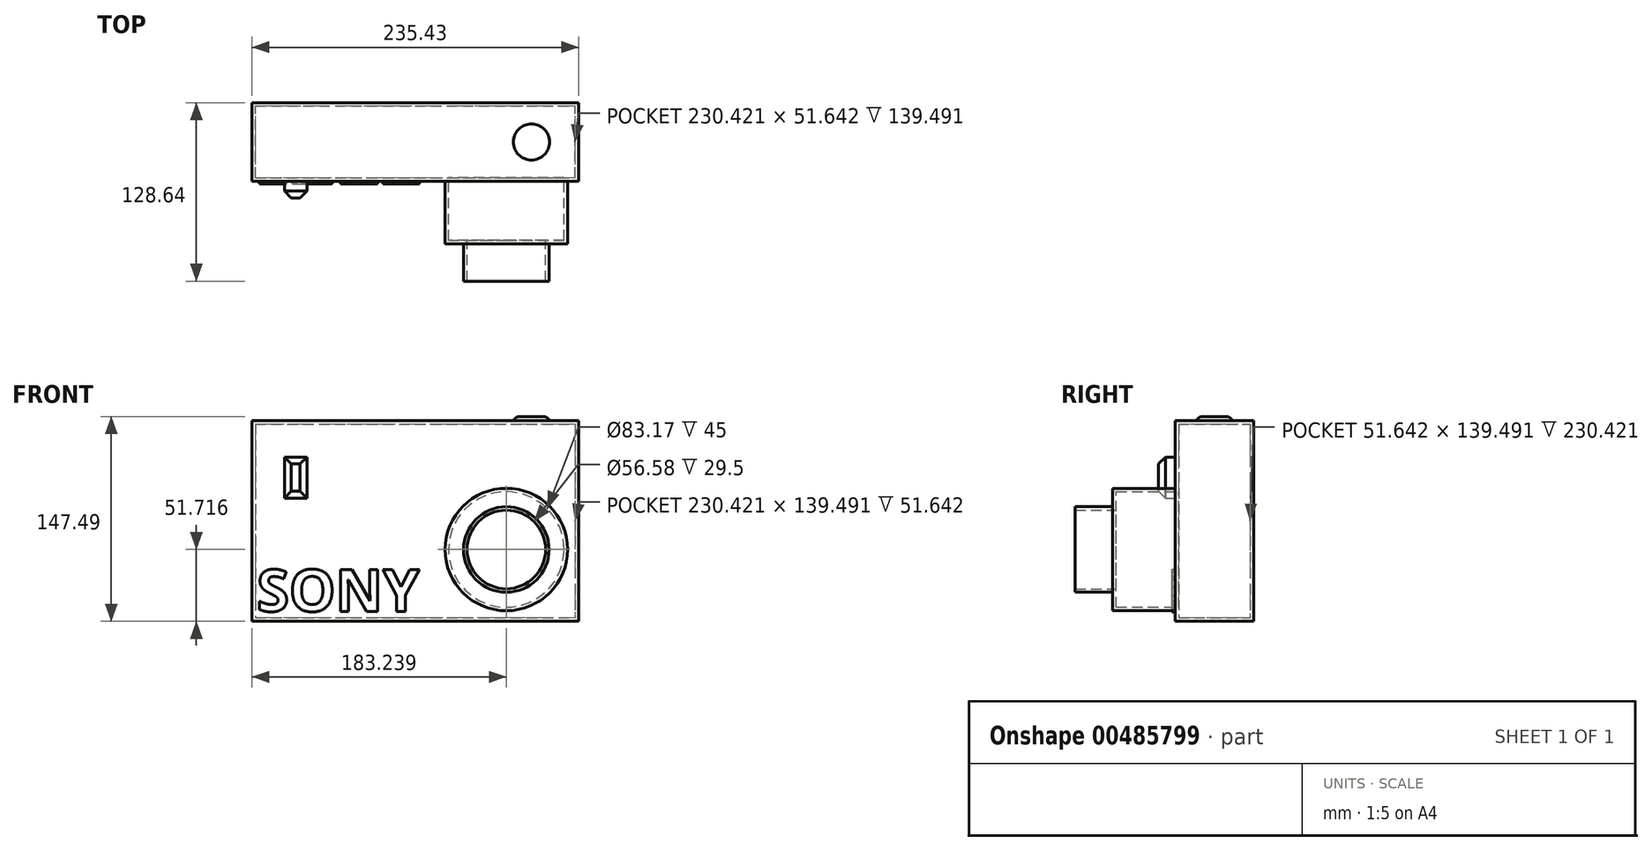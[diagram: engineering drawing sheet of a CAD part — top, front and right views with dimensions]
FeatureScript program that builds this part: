
annotation { "Feature Type Name" : "Feature", "Feature Type Description" : "" }
export const myFeature = defineFeature(function(context is Context, id is Id, definition is map)
    precondition{}
    {
        {
            var Q0;
            Q0=qCreatedBy(makeId("Front.planeOp"),FACE);
            var sketch = newSketch(context, id + "F0", { "sketchPlane" : qUnion([Q0])});
            skLineSegment(sketch, "E0.bottom", {"start": v(-116.88, 70.73) * mm, "end": v(118.55, 70.73) * mm});
            skLineSegment(sketch, "E0.top", {"start": v(-116.88, -73.76) * mm, "end": v(118.55, -73.76) * mm});
            skLineSegment(sketch, "E0.left", {"start": v(-116.88, 70.73) * mm, "end": v(-116.88, -73.76) * mm});
            skLineSegment(sketch, "E0.right", {"start": v(118.55, 70.73) * mm, "end": v(118.55, -73.76) * mm});
            skSolve(sketch);
        }
        {
            var Q0;
            Q0 = qSketchRegion(id + "F0", true);
            extrude(context, id + "F1", {"entities" : qUnion([Q0]), "depth" : 56.64 * mm});
        }
        {
            var Q0;
            Q0=makeQuery(id+"F1.opExtrude","CAP_FACE",FACE,{"disambiguationData":[OSD([sQuery(id+"F0.wireOp",EDGE,"E0.bottom"),sQuery(id+"F0.wireOp",EDGE,"E0.top"),sQuery(id+"F0.wireOp",EDGE,"E0.left"),sQuery(id+"F0.wireOp",EDGE,"E0.right")])],"isStart":false});
            var sketch = newSketch(context, id + "F2", { "sketchPlane" : qUnion([Q0])});
            skCircle(sketch, "E1", {"center": v(66.36, -22.04) * mm, "radius": 44.08 * mm});
            skSolve(sketch);
        }
        {
            var Q0;
            Q0 = qSketchRegion(id + "F2", true);
            extrude(context, id + "F3", {"entities" : qUnion([Q0]), "operationType" : NewBodyOperationType.ADD, "depth" : 45 * mm});
        }
        {
            var Q0;
            Q0=makeQuery(id+"F3.opExtrude","CAP_FACE",FACE,{"disambiguationData":[OSD([sQuery(id+"F2.wireOp",EDGE,"E1")])],"isStart":false});
            var sketch = newSketch(context, id + "F4", { "sketchPlane" : qUnion([Q0])});
            skCircle(sketch, "E2", {"center": v(66.36, -22.04) * mm, "radius": 30.8 * mm});
            skSolve(sketch);
        }
        {
            var Q0;
            Q0 = qSketchRegion(id + "F4", true);
            extrude(context, id + "F5", {"entities" : qUnion([Q0]), "operationType" : NewBodyOperationType.ADD, "depth" : 27 * mm});
        }
        {
            var Q0;
            Q0=makeQuery(id+"F5.opExtrude","CAP_FACE",FACE,{"disambiguationData":[OSD([sQuery(id+"F4.wireOp",EDGE,"E2")])],"isStart":false});
            shell(context, id + "F6", {"entities" : qUnion([Q0]), "thickness" : 2.5 * mm});
        }
        {
            var Q0;
            Q0=makeQuery(id+"F1.opExtrude","SWEPT_FACE",FACE,{"disambiguationData":[OSD([sQuery(id+"F0.wireOp",EDGE,"E0.bottom")])]});
            var sketch = newSketch(context, id + "F7", { "sketchPlane" : qUnion([Q0])});
            skCircle(sketch, "E3", {"center": v(84.46, -28.32) * mm, "radius": 13.02 * mm});
            skPoint(sketch, "E3.centerSnap0", {"position": v(118.55, -28.32) * mm});
            skSolve(sketch);
        }
        {
            var Q0;
            Q0 = qSketchRegion(id + "F7", true);
            extrude(context, id + "F8", {"entities" : qUnion([Q0]), "operationType" : NewBodyOperationType.ADD, "depth" : 3 * mm});
        }
        {
            var Q0;
            Q0=makeQuery(id+"F8.opExtrude","CAP_EDGE",EDGE,{"disambiguationData":[OSD([sQuery(id+"F7.wireOp",EDGE,"E3")])],"isStart":false});
            fillet(context, id + "F9", {"entities" : qUnion([Q0]), "radius" : 5 * mm, "tangentPropagation" : true, "allowEdgeOverflow" : false});
        }
        {
            var Q0;
            Q0=makeQuery(id+"F1.opExtrude","CAP_FACE",FACE,{"disambiguationData":[OSD([sQuery(id+"F0.wireOp",EDGE,"E0.bottom"),sQuery(id+"F0.wireOp",EDGE,"E0.top"),sQuery(id+"F0.wireOp",EDGE,"E0.left"),sQuery(id+"F0.wireOp",EDGE,"E0.right")])],"isStart":false});
            var sketch = newSketch(context, id + "F10", { "sketchPlane" : qUnion([Q0])});
            skLineSegment(sketch, "E4.bottom", {"start": v(-93.43, 44.56) * mm, "end": v(-77.07, 44.56) * mm});
            skLineSegment(sketch, "E4.top", {"start": v(-93.43, 14.96) * mm, "end": v(-77.07, 14.96) * mm});
            skLineSegment(sketch, "E4.left", {"start": v(-93.43, 44.56) * mm, "end": v(-93.43, 14.96) * mm});
            skLineSegment(sketch, "E4.right", {"start": v(-77.07, 44.56) * mm, "end": v(-77.07, 14.96) * mm});
            skSolve(sketch);
        }
        {
            var Q0;
            Q0 = qSketchRegion(id + "F10", true);
            extrude(context, id + "F11", {"entities" : qUnion([Q0]), "operationType" : NewBodyOperationType.ADD, "depth" : 12 * mm});
        }
        {
            var Q0;
            Q0=makeQuery(id+"F11.opExtrude","CAP_FACE",FACE,{"disambiguationData":[OSD([sQuery(id+"F10.wireOp",EDGE,"E4.bottom"),sQuery(id+"F10.wireOp",EDGE,"E4.top"),sQuery(id+"F10.wireOp",EDGE,"E4.left"),sQuery(id+"F10.wireOp",EDGE,"E4.right")])],"isStart":false});
            chamfer(context, id + "F12", {"entities" : qUnion([Q0]), "width" : 5 * mm, "tangentPropagation" : true});
        }
        {
            var Q0;
            Q0=makeQuery(id+"F1.opExtrude","CAP_FACE",FACE,{"disambiguationData":[OSD([sQuery(id+"F0.wireOp",EDGE,"E0.bottom"),sQuery(id+"F0.wireOp",EDGE,"E0.top"),sQuery(id+"F0.wireOp",EDGE,"E0.left"),sQuery(id+"F0.wireOp",EDGE,"E0.right")])],"isStart":false});
            var sketch = newSketch(context, id + "F13", { "sketchPlane" : qUnion([Q0])});
            skText(sketch, "E5", { "text": "SONY", "fontName": "OpenSans-Bold.ttf"});
            const initialGuessF13  = {"E5": [-0.1133, -0.06657, 1, 0, 0.03027]};
            skSetInitialGuess(sketch, initialGuessF13);
            skSolve(sketch);
        }
        {
            var Q0;
            Q0 = qSketchRegion(id + "F13", true);
            extrude(context, id + "F14", {"entities" : qUnion([Q0]), "operationType" : NewBodyOperationType.ADD, "depth" : 2 * mm});
        }
    });
